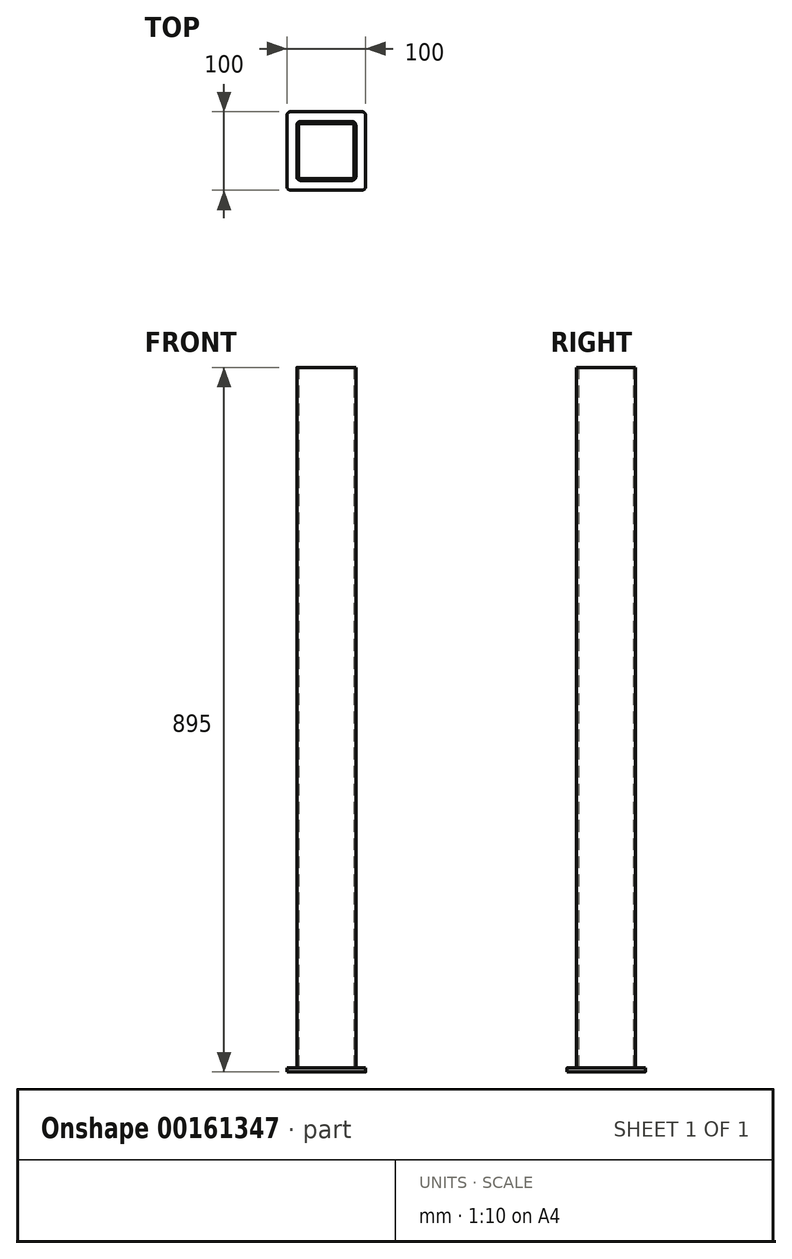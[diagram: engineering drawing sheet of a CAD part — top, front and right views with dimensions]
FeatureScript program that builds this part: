
annotation { "Feature Type Name" : "Feature", "Feature Type Description" : "" }
export const myFeature = defineFeature(function(context is Context, id is Id, definition is map)
    precondition{}
    {
        {
            var Q0;
            Q0=qCreatedBy(makeId("Top.planeOp"),FACE);
            var sketch = newSketch(context, id + "F0", { "sketchPlane" : qUnion([Q0])});
            skLineSegment(sketch, "E0.bottom", {"start": v(37.5, 37.5) * mm, "end": v(-37.5, 37.5) * mm});
            skLineSegment(sketch, "E0.top", {"start": v(37.5, -37.5) * mm, "end": v(-37.5, -37.5) * mm});
            skLineSegment(sketch, "E0.left", {"start": v(37.5, 37.5) * mm, "end": v(37.5, -37.5) * mm});
            skLineSegment(sketch, "E0.right", {"start": v(-37.5, 37.5) * mm, "end": v(-37.5, -37.5) * mm});
            skPoint(sketch, "E0.middle", {"position": v(0, 0) * mm});
            skSolve(sketch);
        }
        {
            var Q0;
            Q0=makeQuery(id+"F0.imprint","IMPRINT",FACE,{"disambiguationData":[TD([[makeQuery(id+"F0.imprint","IMPRINT",EDGE,{"derivedFrom":sQuery(id+"F0.wireOp",EDGE,"E0.bottom")}),1.0]])]});
            extrude(context, id + "F1", {"entities" : qUnion([Q0]), "flatOperationType" : FlatOperationType.REMOVE, "offsetDistance" : 25 * mm, "depth" : 890 * mm, "domain" : OperationDomain.MODEL});
        }
        {
            var Q0;
            Q0=makeQuery(id+"F1.opExtrude","SWEPT_EDGE",EDGE,{"disambiguationData":[OSD([sQuery(id+"F0.wireOp",EDGE,"E0.top"),sQuery(id+"F0.wireOp",EDGE,"E0.right")])]});
            var Q1;
            Q1=makeQuery(id+"F1.opExtrude","SWEPT_EDGE",EDGE,{"disambiguationData":[OSD([sQuery(id+"F0.wireOp",EDGE,"E0.bottom"),sQuery(id+"F0.wireOp",EDGE,"E0.right")])]});
            var Q2;
            Q2=makeQuery(id+"F1.opExtrude","SWEPT_EDGE",EDGE,{"disambiguationData":[OSD([sQuery(id+"F0.wireOp",EDGE,"E0.top"),sQuery(id+"F0.wireOp",EDGE,"E0.left")])]});
            var Q3;
            Q3=makeQuery(id+"F1.opExtrude","SWEPT_EDGE",EDGE,{"disambiguationData":[OSD([sQuery(id+"F0.wireOp",EDGE,"E0.bottom"),sQuery(id+"F0.wireOp",EDGE,"E0.left")])]});
            fillet(context, id + "F2", {"entities" : qUnion([Q0, Q1, Q2, Q3]), "radius" : 5 * mm, "tangentPropagation" : true, "allowEdgeOverflow" : false});
        }
        {
            var Q0;
            Q0=makeQuery(id+"F1.opExtrude","CAP_FACE",FACE,{"disambiguationData":[OSD([sQuery(id+"F0.wireOp",EDGE,"E0.bottom"),sQuery(id+"F0.wireOp",EDGE,"E0.top"),sQuery(id+"F0.wireOp",EDGE,"E0.left"),sQuery(id+"F0.wireOp",EDGE,"E0.right")])],"isStart":true});
            var Q1;
            Q1=makeQuery(id+"F1.opExtrude","CAP_FACE",FACE,{"disambiguationData":[OSD([sQuery(id+"F0.wireOp",EDGE,"E0.bottom"),sQuery(id+"F0.wireOp",EDGE,"E0.top"),sQuery(id+"F0.wireOp",EDGE,"E0.left"),sQuery(id+"F0.wireOp",EDGE,"E0.right")])],"isStart":false});
            shell(context, id + "F3", {"entities" : qUnion([Q0, Q1]), "thickness" : 2.5 * mm});
        }
        {
            var Q0;
            Q0=qCreatedBy(makeId("Top.planeOp"),FACE);
            var sketch = newSketch(context, id + "F4", { "sketchPlane" : qUnion([Q0])});
            skLineSegment(sketch, "E1.bottom", {"start": v(50, 50) * mm, "end": v(-50, 50) * mm});
            skLineSegment(sketch, "E1.top", {"start": v(50, -50) * mm, "end": v(-50, -50) * mm});
            skLineSegment(sketch, "E1.left", {"start": v(50, 50) * mm, "end": v(50, -50) * mm});
            skLineSegment(sketch, "E1.right", {"start": v(-50, 50) * mm, "end": v(-50, -50) * mm});
            skPoint(sketch, "E1.middle", {"position": v(0, 0) * mm});
            skSolve(sketch);
        }
        {
            var Q0;
            Q0=makeQuery(id+"F4.imprint","IMPRINT",FACE,{"disambiguationData":[TD([[makeQuery(id+"F4.imprint","IMPRINT",EDGE,{"derivedFrom":sQuery(id+"F4.wireOp",EDGE,"E1.bottom")}),1.0]])]});
            extrude(context, id + "F5", {"entities" : qUnion([Q0]), "operationType" : NewBodyOperationType.ADD, "oppositeDirection" : true, "depth" : 5 * mm});
        }
        {
            var Q0;
            Q0=makeQuery(id+"F5.opExtrude","SWEPT_EDGE",EDGE,{"disambiguationData":[OSD([sQuery(id+"F4.wireOp",EDGE,"E1.top"),sQuery(id+"F4.wireOp",EDGE,"E1.left")])]});
            var Q1;
            Q1=makeQuery(id+"F5.opExtrude","SWEPT_EDGE",EDGE,{"disambiguationData":[OSD([sQuery(id+"F4.wireOp",EDGE,"E1.bottom"),sQuery(id+"F4.wireOp",EDGE,"E1.left")])]});
            var Q2;
            Q2=makeQuery(id+"F5.opExtrude","SWEPT_EDGE",EDGE,{"disambiguationData":[OSD([sQuery(id+"F4.wireOp",EDGE,"E1.top"),sQuery(id+"F4.wireOp",EDGE,"E1.right")])]});
            var Q3;
            Q3=makeQuery(id+"F5.opExtrude","SWEPT_EDGE",EDGE,{"disambiguationData":[OSD([sQuery(id+"F4.wireOp",EDGE,"E1.bottom"),sQuery(id+"F4.wireOp",EDGE,"E1.right")])]});
            fillet(context, id + "F6", {"entities" : qUnion([Q0, Q1, Q2, Q3]), "radius" : 5 * mm, "tangentPropagation" : true, "allowEdgeOverflow" : false});
        }
    });
